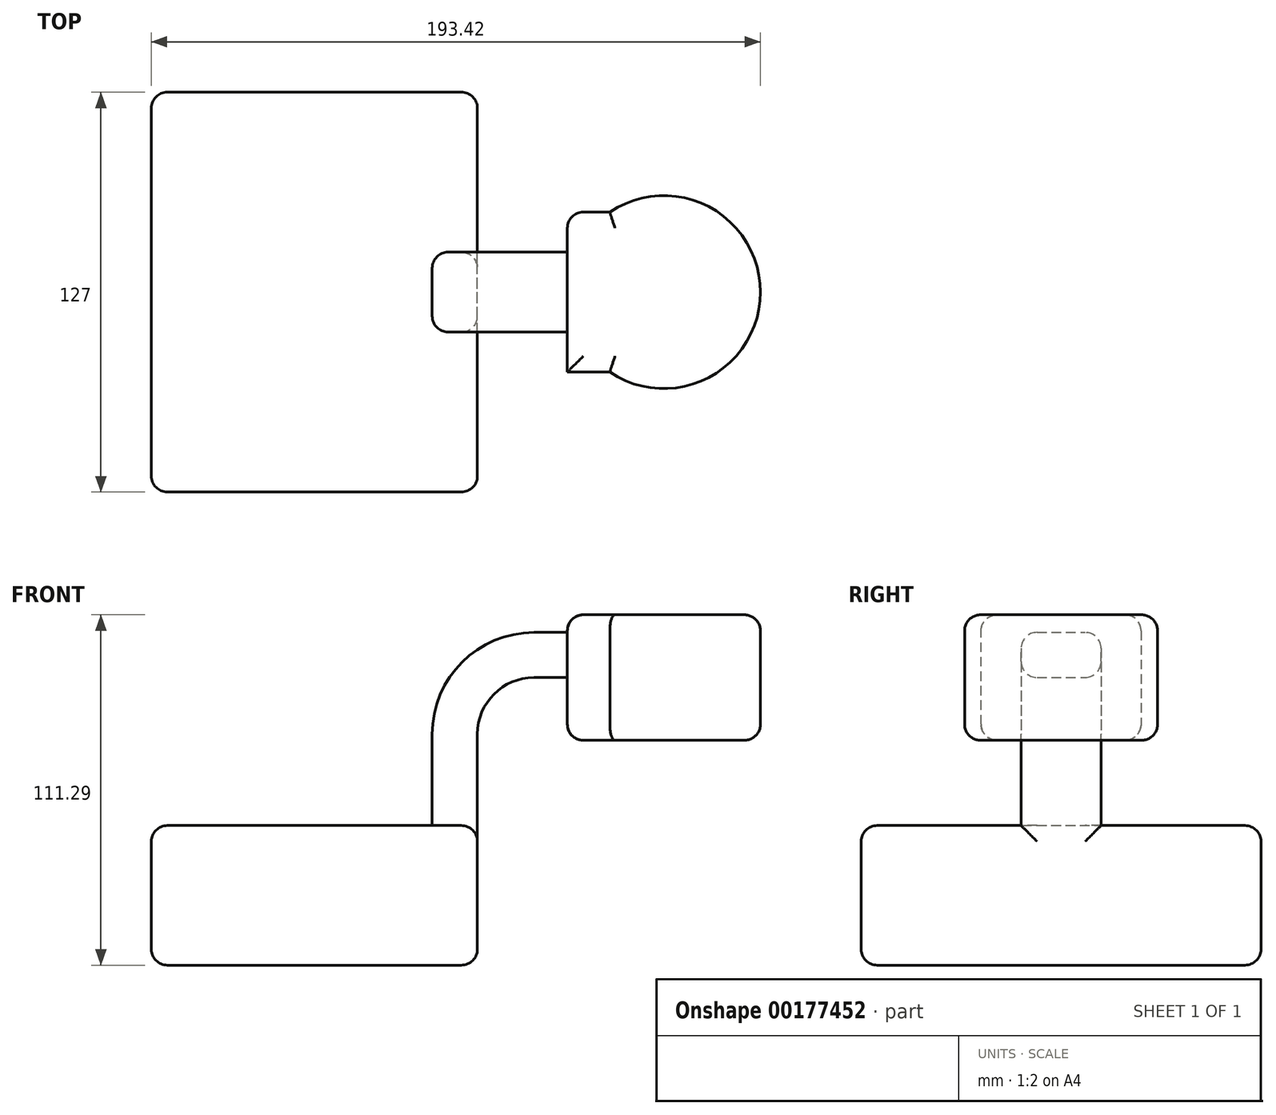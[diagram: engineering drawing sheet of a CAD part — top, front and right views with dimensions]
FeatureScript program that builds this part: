
annotation { "Feature Type Name" : "Feature", "Feature Type Description" : "" }
export const myFeature = defineFeature(function(context is Context, id is Id, definition is map)
    precondition{}
    {
        {
            var Q0;
            Q0=qCreatedBy(makeId("Front.planeOp"),FACE);
            var sketch = newSketch(context, id + "F0", { "sketchPlane" : qUnion([Q0])});
            skLineSegment(sketch, "E0.bottom", {"start": v(-51.78, 22.17) * mm, "end": v(51.78, 22.17) * mm});
            skLineSegment(sketch, "E0.top", {"start": v(-51.78, -22.17) * mm, "end": v(51.78, -22.17) * mm});
            skLineSegment(sketch, "E0.left", {"start": v(-51.78, 22.17) * mm, "end": v(-51.78, -22.17) * mm});
            skLineSegment(sketch, "E0.right", {"start": v(51.78, 22.17) * mm, "end": v(51.78, -22.17) * mm});
            skPoint(sketch, "E0.middle", {"position": v(0, 0) * mm});
            skLineSegment(sketch, "E1.bottom", {"start": v(80.34, 49.25) * mm, "end": v(141.64, 49.25) * mm});
            skLineSegment(sketch, "E1.top", {"start": v(80.34, 89.12) * mm, "end": v(141.64, 89.12) * mm});
            skLineSegment(sketch, "E1.left", {"start": v(80.34, 49.25) * mm, "end": v(80.34, 89.12) * mm});
            skLineSegment(sketch, "E1.right", {"start": v(141.64, 49.25) * mm, "end": v(141.64, 89.12) * mm});
            skPoint(sketch, "E1.middle", {"position": v(111, 69.19) * mm});
            skLineSegment(sketch, "E2", {"start": v(51.78, 22.17) * mm, "end": v(51.78, 51.23) * mm});
            skArc(sketch, "E3", {"start": v(51.78, 51.23) * mm, "mid": v(57.04, 63.93) * mm, "end": v(69.73, 69.19) * mm});
            skLineSegment(sketch, "E4", {"start": v(69.73, 69.19) * mm, "end": v(99.69, 69.19) * mm});
            skPoint(sketch, "E4.endSnap0", {"position": v(80.34, 69.19) * mm});
            skLineSegment(sketch, "E5.0", {"start": v(69.73, 83.52) * mm, "end": v(99.69, 83.52) * mm});
            skArc(sketch, "E5.1", {"start": v(37.44, 51.23) * mm, "mid": v(46.9, 74.06) * mm, "end": v(69.73, 83.52) * mm});
            skLineSegment(sketch, "E5.2", {"start": v(37.44, 22.17) * mm, "end": v(37.44, 51.23) * mm});
            skLineSegment(sketch, "E6", {"start": v(111, 49.25) * mm, "end": v(111, 89.12) * mm});
            skSolve(sketch);
        }
        {
            var Q0;
            Q0=makeQuery(id+"F0.imprint","IMPRINT",FACE,{"disambiguationData":[TD([[makeQuery(id+"F0.imprint","IMPRINT",EDGE,{"derivedFrom":sQuery(id+"F0.wireOp",EDGE,"E0.top")}),1.0]])]});
            extrude(context, id + "F1", {"entities" : qUnion([Q0]), "endBound" : BoundingType.SYMMETRIC, "depth" : 127 * mm});
        }
        {
            var Q0;
            {var subQ2=sQuery(id+"F0.wireOp",EDGE,"E2");Q0=makeQuery(id+"F0.imprint","IMPRINT",FACE,{"disambiguationData":[TD([[makeQuery(id+"F0.imprint","IMPRINT",EDGE,{"derivedFrom":subQ2}),1.0]])]});}
            extrude(context, id + "F2", {"entities" : qUnion([Q0]), "operationType" : NewBodyOperationType.ADD, "endBound" : BoundingType.SYMMETRIC, "depth" : 25.4 * mm});
        }
        {
            var Q0;
            {var subQ7=sQuery(id+"F0.wireOp",EDGE,"E6");Q0=makeQuery(id+"F0.imprint","IMPRINT",FACE,{"disambiguationData":[TD([[makeQuery(id+"F0.imprint","IMPRINT",EDGE,{"derivedFrom":subQ7}),1.0]])]});}
            extrude(context, id + "F3", {"entities" : qUnion([Q0]), "operationType" : NewBodyOperationType.ADD, "endBound" : BoundingType.SYMMETRIC, "depth" : 50.8 * mm});
        }
        {
            var Q0;
            {var subQ0=sQuery(id+"F0.wireOp",EDGE,"E1.right");Q0=makeQuery(id+"F0.imprint","IMPRINT",FACE,{"disambiguationData":[TD([[makeQuery(id+"F0.imprint","IMPRINT",EDGE,{"derivedFrom":subQ0}),1.0]])]});}
            var Q1;
            Q1=sQuery(id+"F0.wireOp",EDGE,"E6");
            revolve(context, id + "F4", {"operationType" : NewBodyOperationType.ADD, "entities" : qUnion([Q0]), "axis" : qUnion([Q1]), "revolveType" : RevolveType.FULL});
        }
        {
            var Q0;
            Q0=makeQuery(id+"F2.opExtrude","CAP_EDGE",EDGE,{"disambiguationData":[OSD([sQuery(id+"F0.wireOp",EDGE,"E2")])],"isStart":true});
            var Q1;
            Q1=makeQuery(id+"F2.opExtrude","CAP_EDGE",EDGE,{"disambiguationData":[OSD([sQuery(id+"F0.wireOp",EDGE,"E5.1")])],"isStart":true});
            var Q2;
            Q2=makeQuery(id+"F2.opExtrude","CAP_EDGE",EDGE,{"disambiguationData":[OSD([sQuery(id+"F0.wireOp",EDGE,"E5.1")])],"isStart":false});
            var Q3;
            Q3=makeQuery(id+"F3.opExtrude","CAP_EDGE",EDGE,{"disambiguationData":[OSD([sQuery(id+"F0.wireOp",EDGE,"E1.left")])],"isStart":true});
            var Q4;
            Q4=makeQuery(id+"F4.opRevolve","SWEPT_EDGE",EDGE,{"disambiguationData":[OSD([sQuery(id+"F0.wireOp",EDGE,"E1.top"),sQuery(id+"F0.wireOp",EDGE,"E1.right")])]});
            var Q5;
            Q5=makeQuery(id+"F3.opExtrude","CAP_EDGE",EDGE,{"disambiguationData":[OSD([sQuery(id+"F0.wireOp",EDGE,"E1.top")])],"isStart":true});
            var Q6;
            Q6=makeQuery(id+"F3.opExtrude","SWEPT_EDGE",EDGE,{"disambiguationData":[OSD([sQuery(id+"F0.wireOp",EDGE,"E1.top"),sQuery(id+"F0.wireOp",EDGE,"E1.left")])]});
            var Q7;
            Q7=makeQuery(id+"F3.opExtrude","CAP_EDGE",EDGE,{"disambiguationData":[OSD([sQuery(id+"F0.wireOp",EDGE,"E1.top")])],"isStart":false});
            var Q8;
            Q8=makeQuery(id+"F3.opExtrude","CAP_EDGE",EDGE,{"disambiguationData":[OSD([sQuery(id+"F0.wireOp",EDGE,"E1.bottom")])],"isStart":true});
            var Q9;
            Q9=makeQuery(id+"F4.opRevolve","SWEPT_EDGE",EDGE,{"disambiguationData":[OSD([sQuery(id+"F0.wireOp",EDGE,"E1.bottom"),sQuery(id+"F0.wireOp",EDGE,"E1.right")])]});
            var Q10;
            Q10=makeQuery(id+"F3.opExtrude","CAP_EDGE",EDGE,{"disambiguationData":[OSD([sQuery(id+"F0.wireOp",EDGE,"E1.bottom")])],"isStart":false});
            var Q11;
            Q11=makeQuery(id+"F3.opExtrude","SWEPT_EDGE",EDGE,{"disambiguationData":[OSD([sQuery(id+"F0.wireOp",EDGE,"E1.bottom"),sQuery(id+"F0.wireOp",EDGE,"E1.left")])]});
            var Q12;
            Q12=makeQuery(id+"F2.opExtrude","CAP_EDGE",EDGE,{"disambiguationData":[OSD([sQuery(id+"F0.wireOp",EDGE,"E2")])],"isStart":false});
            var Q13;
            Q13=makeQuery(id+"F2.opExtrude","CAP_EDGE",EDGE,{"disambiguationData":[OSD([sQuery(id+"F0.wireOp",EDGE,"E3")])],"isStart":true});
            var Q14;
            Q14=makeQuery(id+"F1.opExtrude","CAP_EDGE",EDGE,{"disambiguationData":[OSD([sQuery(id+"F0.wireOp",EDGE,"E0.bottom")])],"isStart":true});
            var Q15;
            Q15=makeQuery(id+"F1.opExtrude","SWEPT_EDGE",EDGE,{"disambiguationData":[OSD([sQuery(id+"F0.wireOp",EDGE,"E0.bottom"),sQuery(id+"F0.wireOp",EDGE,"E0.left")])]});
            var Q16;
            Q16=makeQuery(id+"F1.opExtrude","CAP_EDGE",EDGE,{"disambiguationData":[OSD([sQuery(id+"F0.wireOp",EDGE,"E0.left")])],"isStart":true});
            var Q17;
            Q17=makeQuery(id+"F1.opExtrude","SWEPT_EDGE",EDGE,{"disambiguationData":[OSD([sQuery(id+"F0.wireOp",EDGE,"E0.top"),sQuery(id+"F0.wireOp",EDGE,"E0.left")])]});
            var Q18;
            Q18=makeQuery(id+"F1.opExtrude","CAP_EDGE",EDGE,{"disambiguationData":[OSD([sQuery(id+"F0.wireOp",EDGE,"E0.top")])],"isStart":true});
            var Q19;
            {var subQ0=sQuery(id+"F0.wireOp",EDGE,"E2");var subQ1=sQuery(id+"F0.wireOp",EDGE,"E0.bottom");var subQ2=sQuery(id+"F0.wireOp",EDGE,"E0.right");Q19=makeQuery(id+"F2.boolean.opBoolean","SPLIT",EDGE,{"disambiguationData":[TD([makeQuery(id+"F1.opExtrude","CAP_FACE",FACE,{"disambiguationData":[OSD([subQ1,sQuery(id+"F0.wireOp",EDGE,"E0.top"),sQuery(id+"F0.wireOp",EDGE,"E0.left"),subQ2])],"isStart":true})])],"derivedFrom":makeQuery(id+"F1.opExtrude","SWEPT_EDGE",EDGE,{"disambiguationData":[OSD([subQ1,subQ2,subQ0])]})});}
            var Q20;
            Q20=makeQuery(id+"F1.opExtrude","CAP_EDGE",EDGE,{"disambiguationData":[OSD([sQuery(id+"F0.wireOp",EDGE,"E0.bottom")])],"isStart":false});
            var Q21;
            Q21=makeQuery(id+"F1.opExtrude","CAP_EDGE",EDGE,{"disambiguationData":[OSD([sQuery(id+"F0.wireOp",EDGE,"E0.left")])],"isStart":false});
            var Q22;
            Q22=makeQuery(id+"F1.opExtrude","CAP_EDGE",EDGE,{"disambiguationData":[OSD([sQuery(id+"F0.wireOp",EDGE,"E0.right")])],"isStart":true});
            var Q23;
            Q23=makeQuery(id+"F1.opExtrude","CAP_EDGE",EDGE,{"disambiguationData":[OSD([sQuery(id+"F0.wireOp",EDGE,"E0.top")])],"isStart":false});
            var Q24;
            Q24=makeQuery(id+"F1.opExtrude","SWEPT_EDGE",EDGE,{"disambiguationData":[OSD([sQuery(id+"F0.wireOp",EDGE,"E0.top"),sQuery(id+"F0.wireOp",EDGE,"E0.right")])]});
            var Q25;
            Q25=makeQuery(id+"F1.opExtrude","CAP_EDGE",EDGE,{"disambiguationData":[OSD([sQuery(id+"F0.wireOp",EDGE,"E0.right")])],"isStart":false});
            var Q26;
            {var subQ0=sQuery(id+"F0.wireOp",EDGE,"E2");var subQ1=sQuery(id+"F0.wireOp",EDGE,"E0.bottom");var subQ2=sQuery(id+"F0.wireOp",EDGE,"E0.right");Q26=makeQuery(id+"F2.boolean.opBoolean","SPLIT",EDGE,{"disambiguationData":[TD([makeQuery(id+"F1.opExtrude","CAP_FACE",FACE,{"disambiguationData":[OSD([subQ1,sQuery(id+"F0.wireOp",EDGE,"E0.top"),sQuery(id+"F0.wireOp",EDGE,"E0.left"),subQ2])],"isStart":false})])],"derivedFrom":makeQuery(id+"F1.opExtrude","SWEPT_EDGE",EDGE,{"disambiguationData":[OSD([subQ1,subQ2,subQ0])]})});}
            fillet(context, id + "F5", {"entities" : qUnion([Q0, Q1, Q2, Q3, Q4, Q5, Q6, Q7, Q8, Q9, Q10, Q11, Q12, Q13, Q14, Q15, Q16, Q17, Q18, Q19, Q20, Q21, Q22, Q23, Q24, Q25, Q26]), "radius" : 5.08 * mm, "tangentPropagation" : true, "allowEdgeOverflow" : false});
        }
    });
